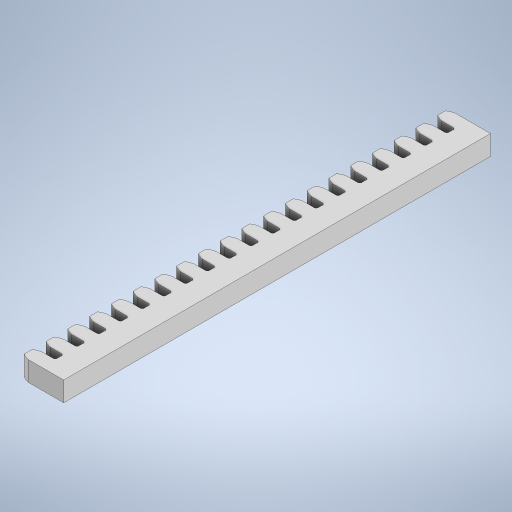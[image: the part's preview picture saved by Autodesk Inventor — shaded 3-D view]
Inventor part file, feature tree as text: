
AUTODESK INVENTOR PART (.ipt)
format: ipt  version: 2024 (Build 280153000, 153)  size: 445,952 bytes
history: native  units: in
note: dims shown in document units (in); Inventor stores cm internally (conversion verified against a paired STEP export)
features: extrude x1, sketch x1
ambient origin geometry x8: Origin, YZ Plane, XZ Plane, XY Plane, X Axis, Y Axis, Z Axis, Center Point
bodies: Solid1 (feature_tree)
feature tree (2):
  extrude  "Extrusion1"  Depth=0.1181in
  sketch  "Sketch3"  dims[d16=0.0236in d17=0.0472in d18=0.1181in d19=0.1181in d21=2.5591in d23=7.874in d25=0.1299in d26=0.3937in d28=0.3937in d30=0.1181in d31=0.0in]
